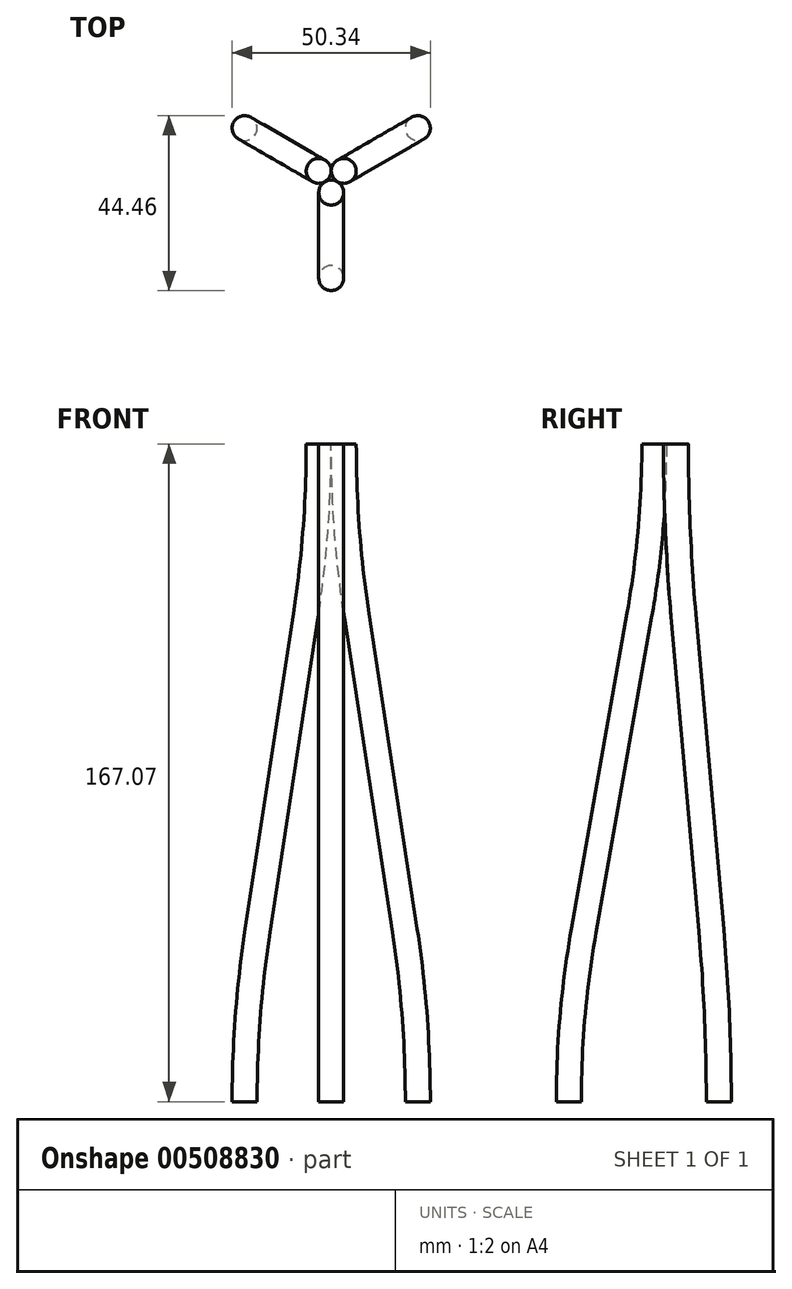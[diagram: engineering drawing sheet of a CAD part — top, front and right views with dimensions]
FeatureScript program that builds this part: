
annotation { "Feature Type Name" : "Feature", "Feature Type Description" : "" }
export const myFeature = defineFeature(function(context is Context, id is Id, definition is map)
    precondition{}
    {
        {
            var Q0;
            Q0=qCreatedBy(makeId("Right.planeOp"),FACE);
            var sketch = newSketch(context, id + "F0", { "sketchPlane" : qUnion([Q0])});
            skLineSegment(sketch, "E0", {"start": v(0, 0) * mm, "end": v(0, 179.6) * mm});
            skLineSegment(sketch, "E1", {"start": v(0, 179.6) * mm, "end": v(-169.33, -59.87) * mm});
            skLineSegment(sketch, "E2", {"start": v(-169.33, -59.87) * mm, "end": v(0, 0) * mm});
            skLineSegment(sketch, "E3", {"start": v(-169.33, -59.87) * mm, "end": v(84.67, -59.87) * mm, "construction": true});
            skLineSegment(sketch, "E4", {"start": v(0, 179.6) * mm, "end": v(84.67, -59.87) * mm, "construction": true});
            skLineSegment(sketch, "E5", {"start": v(0, 0) * mm, "end": v(84.67, -59.87) * mm, "construction": true});
            skLineSegment(sketch, "E6", {"start": v(0, 0) * mm, "end": v(0, -59.87) * mm, "construction": true});
            skCircle(sketch, "E7", {"center": v(-84.67, -59.87) * mm, "radius": 84.67 * mm, "construction": true});
            skCircle(sketch, "E8", {"center": v(0, -59.87) * mm, "radius": 84.67 * mm, "construction": true});
            skArc(sketch, "E9", {"start": v(-169.33, -59.87) * mm, "mid": v(-46.6, 32.96) * mm, "end": v(0, 179.6) * mm, "construction": true});
            skLineSegment(sketch, "E10", {"start": v(0, 179.6) * mm, "end": v(-254, 179.6) * mm, "construction": true});
            skLineSegment(sketch, "E11", {"start": v(-169.33, -59.87) * mm, "end": v(-254, 179.6) * mm, "construction": true});
            skSolve(sketch);
        }
        {
            var Q0;
            Q0=qCreatedBy(makeId("Right.planeOp"),FACE);
            var sketch = newSketch(context, id + "F1", { "sketchPlane" : qUnion([Q0])});
            skPoint(sketch, "E12.0", {"position": v(-254, 179.6) * mm});
            skPoint(sketch, "E13.0", {"position": v(-169.33, -59.87) * mm});
            skPoint(sketch, "E14.0", {"position": v(0, 0) * mm});
            skArc(sketch, "E15", {"start": v(-169.33, -59.87) * mm, "mid": v(-46.6, 32.96) * mm, "end": v(0, 179.6) * mm, "construction": true});
            skLineSegment(sketch, "E16", {"start": v(0, 179.6) * mm, "end": v(-254, 179.6) * mm, "construction": true});
            skLineSegment(sketch, "E17", {"start": v(-169.33, -59.87) * mm, "end": v(-254, 179.6) * mm, "construction": true});
            skCircle(sketch, "E18", {"center": v(-3.67, 0) * mm, "radius": 3.18 * mm, "construction": true});
            skCircle(sketch, "E19.1.0", {"center": v(1.83, -3.18) * mm, "radius": 3.18 * mm, "construction": true});
            skCircle(sketch, "E19.2.0", {"center": v(1.83, 3.18) * mm, "radius": 3.18 * mm, "construction": true});
            skLineSegment(sketch, "E20", {"start": v(1.83, 3.18) * mm, "end": v(1.83, -3.18) * mm, "construction": true});
            skLineSegment(sketch, "E21", {"start": v(-3.67, 0) * mm, "end": v(1.83, 0) * mm, "construction": true});
            skLineSegment(sketch, "E22", {"start": v(-3.67, 0) * mm, "end": v(-12.7, 0) * mm, "construction": true});
            skCircle(sketch, "E23", {"center": v(-12.7, 0) * mm, "radius": 3.18 * mm, "construction": true});
            skCircle(sketch, "E24.1.0", {"center": v(6.35, -11) * mm, "radius": 3.18 * mm, "construction": true});
            skCircle(sketch, "E24.2.0", {"center": v(6.35, 11) * mm, "radius": 3.18 * mm, "construction": true});
            skLineSegment(sketch, "E25", {"start": v(6.35, 11) * mm, "end": v(6.35, -11) * mm, "construction": true});
            skLineSegment(sketch, "E26", {"start": v(1.83, 0) * mm, "end": v(6.35, 0) * mm, "construction": true});
            skArc(sketch, "E27.0", {"start": v(-7.47, 136.14) * mm, "mid": v(-4.62, 157.79) * mm, "end": v(-3.67, 179.6) * mm});
            skLineSegment(sketch, "E28", {"start": v(-254, 179.6) * mm, "end": v(-7.47, 136.14) * mm, "construction": true});
            skArc(sketch, "E29", {"start": v(-175.24, -43.17) * mm, "mid": v(-61.07, 43.18) * mm, "end": v(-17.7, 179.6) * mm, "construction": true});
            skLineSegment(sketch, "E30", {"start": v(-21.3, 138.57) * mm, "end": v(-17.7, 179.6) * mm, "construction": true});
            skSolve(sketch);
        }
        {
            var Q0;
            Q0=qCreatedBy(makeId("Right.planeOp"),FACE);
            var sketch = newSketch(context, id + "F2", { "sketchPlane" : qUnion([Q0])});
            skPoint(sketch, "E31.0", {"position": v(-3.67, 179.6) * mm});
            skPoint(sketch, "E31.1", {"position": v(-7.47, 136.14) * mm});
            skPoint(sketch, "E31.2", {"position": v(-254, 179.6) * mm});
            skPoint(sketch, "E31.3", {"position": v(0, 0) * mm});
            skPoint(sketch, "E31.4", {"position": v(-12.7, 0) * mm});
            skArc(sketch, "E32", {"start": v(-7.47, 136.14) * mm, "mid": v(-4.62, 157.79) * mm, "end": v(-3.67, 179.6) * mm});
            skLineSegment(sketch, "E33", {"start": v(-7.47, 136.14) * mm, "end": v(-8.9, 128.04) * mm});
            skLineSegment(sketch, "E34", {"start": v(-8.18, 132.09) * mm, "end": v(-8.18, 84.57) * mm, "construction": true});
            skArc(sketch, "E35.1.0", {"start": v(-8.9, 128.04) * mm, "mid": v(-11.75, 106.39) * mm, "end": v(-12.7, 84.57) * mm});
            skPoint(sketch, "E35.center", {"position": v(-8.18, 132.09) * mm});
            skSolve(sketch);
        }
        {
            var Q0;
            Q0=qCreatedBy(makeId("Right.planeOp"),FACE);
            var sketch = newSketch(context, id + "F3", { "sketchPlane" : qUnion([Q0])});
            skPoint(sketch, "E36.0", {"position": v(0, 0) * mm});
            skPoint(sketch, "E37.0", {"position": v(-3.67, 179.6) * mm});
            skPoint(sketch, "E37.1", {"position": v(-7.47, 136.14) * mm});
            skPoint(sketch, "E37.2", {"position": v(-254, 179.6) * mm});
            skArc(sketch, "E38", {"start": v(-7.47, 136.14) * mm, "mid": v(-4.62, 157.79) * mm, "end": v(-3.67, 179.6) * mm});
            skLineSegment(sketch, "E39", {"start": v(-7.47, 136.14) * mm, "end": v(-21.6, 56.01) * mm});
            skLineSegment(sketch, "E40", {"start": v(-14.53, 96.07) * mm, "end": v(-14.53, 12.54) * mm, "construction": true});
            skArc(sketch, "E41.1.0", {"start": v(-21.6, 56.01) * mm, "mid": v(-24.45, 34.36) * mm, "end": v(-25.4, 12.54) * mm});
            skPoint(sketch, "E41.center", {"position": v(-14.53, 96.07) * mm});
            skLineSegment(sketch, "E42", {"start": v(0, 0) * mm, "end": v(-25.4, 0) * mm, "construction": true});
            skSolve(sketch);
        }
        {
            var Q0;
            Q0=sQuery(id+"F0.wireOp",VERTEX,"E8.center");
            var Q1;
            Q1=qCreatedBy(makeId("Top.planeOp"),FACE);
            cPlane(context, id + "F4", {"entities" : qUnion([Q0, Q1]), "cplaneType" : CPlaneType.PLANE_POINT, "offset" : 25.4 * mm, "width" : 152.4 * mm, "height" : 152.4 * mm});
        }
        {
            var Q0;
            Q0=qCreatedBy(id+"F4.planeOp",FACE);
            var sketch = newSketch(context, id + "F5", { "sketchPlane" : qUnion([Q0])});
            skCircle(sketch, "E43.cCircle", {"center": v(0, 0) * mm, "radius": 169.33 * mm, "construction": true});
            skLineSegment(sketch, "E43.0", {"start": v(0, -169.33) * mm, "end": v(-146.65, 84.67) * mm, "construction": true});
            skLineSegment(sketch, "E43.1", {"start": v(-146.65, 84.67) * mm, "end": v(146.65, 84.67) * mm, "construction": true});
            skLineSegment(sketch, "E43.2", {"start": v(146.65, 84.67) * mm, "end": v(0, -169.33) * mm, "construction": true});
            skSolve(sketch);
        }
        {
            var Q0;
            Q0=sQuery(id+"F0.wireOp",VERTEX,"E6.start");
            var Q1;
            Q1=sQuery(id+"F5.wireOp",VERTEX,"E43.1.start");
            var Q2;
            Q2=sQuery(id+"F5.wireOp",VERTEX,"E43.2.start");
            cPlane(context, id + "F6", {"entities" : qUnion([Q0, Q1, Q2]), "cplaneType" : CPlaneType.THREE_POINT, "offset" : 25.4 * mm, "width" : 152.4 * mm, "height" : 152.4 * mm});
        }
        {
            var Q0;
            Q0=qCreatedBy(id+"F6.planeOp",FACE);
            var sketch = newSketch(context, id + "F7", { "sketchPlane" : qUnion([Q0])});
            skLineSegment(sketch, "E44", {"start": v(-146.65, 103.7) * mm, "end": v(0, 0) * mm});
            skLineSegment(sketch, "E45", {"start": v(0, 0) * mm, "end": v(146.65, 103.7) * mm});
            skLineSegment(sketch, "E46", {"start": v(146.65, 103.7) * mm, "end": v(-146.65, 103.7) * mm});
            skLineSegment(sketch, "E47", {"start": v(0, 103.7) * mm, "end": v(0, 0) * mm});
            skSolve(sketch);
        }
        {
            var Q0;
            Q0=sQuery(id+"F7.wireOp",VERTEX,"E46.end");
            var Q1;
            Q1=sQuery(id+"F7.wireOp",VERTEX,"E46.start");
            var Q2;
            Q2=sQuery(id+"F0.wireOp",VERTEX,"E4.start");
            cPlane(context, id + "F8", {"entities" : qUnion([Q0, Q1, Q2]), "cplaneType" : CPlaneType.THREE_POINT, "offset" : 25.4 * mm, "width" : 152.4 * mm, "height" : 152.4 * mm});
        }
        {
            var Q0;
            Q0=sQuery(id+"F1.wireOp",VERTEX,"E27.0.end");
            var Q1;
            Q1=qCreatedBy(makeId("Top.planeOp"),FACE);
            cPlane(context, id + "F9", {"entities" : qUnion([Q0, Q1]), "cplaneType" : CPlaneType.PLANE_POINT, "offset" : 25.4 * mm, "width" : 152.4 * mm, "height" : 152.4 * mm});
        }
        {
            var Q0;
            Q0=qCreatedBy(id+"F9.planeOp",FACE);
            var sketch = newSketch(context, id + "F10", { "sketchPlane" : qUnion([Q0])});
            skPoint(sketch, "E48.0", {"position": v(0, -3.67) * mm});
            skCircle(sketch, "E49", {"center": v(0, -3.67) * mm, "radius": 3.18 * mm});
            skSolve(sketch);
        }
        {
            var Q0;
            Q0=makeQuery(id+"F10.imprint","IMPRINT",FACE,{"disambiguationData":[TD([[makeQuery(id+"F10.imprint","IMPRINT",EDGE,{"derivedFrom":sQuery(id+"F10.wireOp",EDGE,"E49")}),1.0]])]});
            var Q1;
            Q1=sQuery(id+"F3.wireOp",EDGE,"E38");
            var Q2;
            Q2=sQuery(id+"F3.wireOp",EDGE,"E39");
            var Q3;
            Q3=sQuery(id+"F3.wireOp",EDGE,"E41.1.0");
            sweep(context, id + "F11", {"profiles" : qUnion([Q0]), "path" : qUnion([Q1, Q2, Q3])});
        }
        {
            var Q0;
            Q0=makeQuery(id+"F11.opSweep","SWEPT_BODY",BODY,{"disambiguationData":[OSD([sQuery(id+"F3.wireOp",EDGE,"E41.1.0"),sQuery(id+"F10.wireOp",EDGE,"E49")])]});
            var Q1;
            Q1=sQuery(id+"F0.wireOp",EDGE,"E0");
            circularPattern(context, id + "F12", {"entities" : qUnion([Q0]), "axis" : qUnion([Q1]), "angle" : 360 * degree, "instanceCount" : 3, "equalSpace" : true, "computeTransformsWithoutBuiltin" : true});
        }
    });
